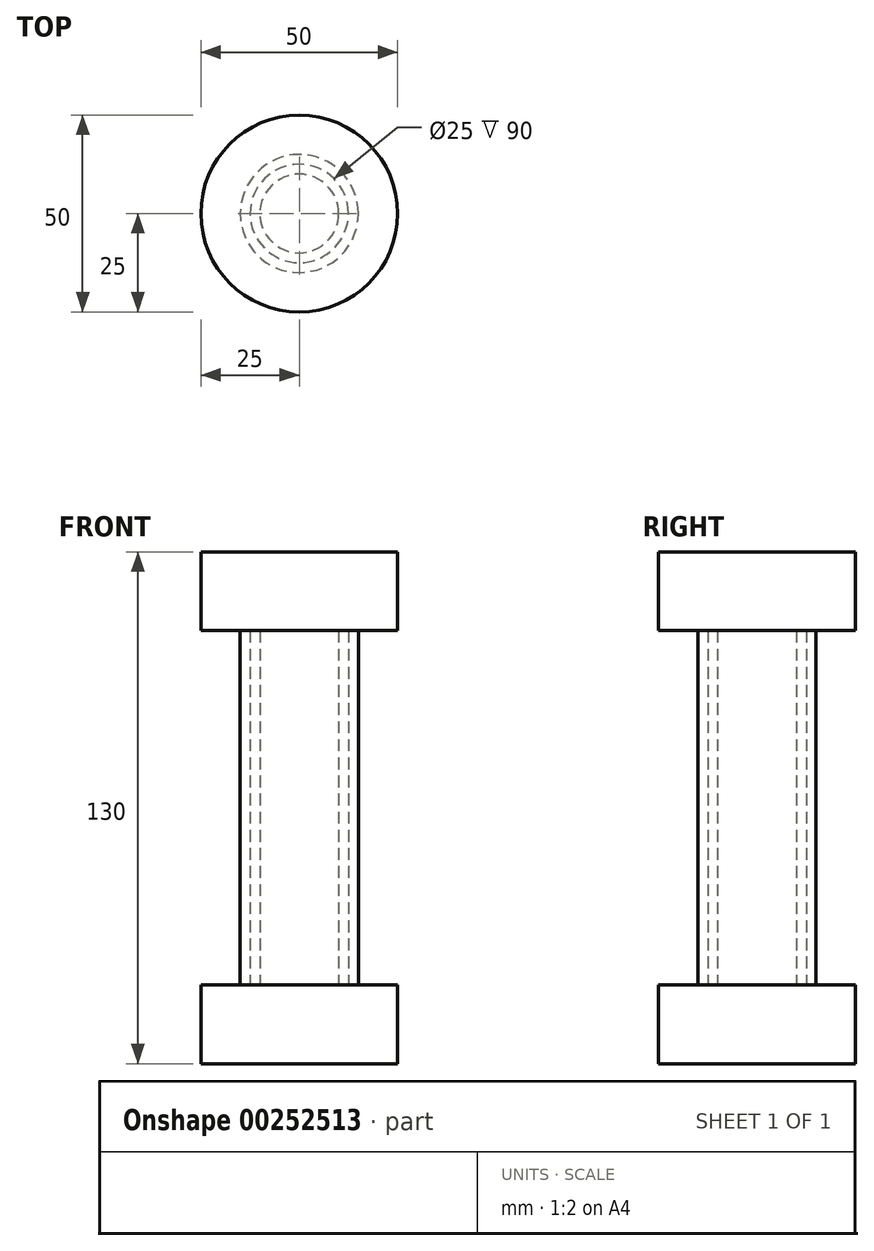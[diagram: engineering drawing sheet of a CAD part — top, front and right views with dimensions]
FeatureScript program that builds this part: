
annotation { "Feature Type Name" : "Feature", "Feature Type Description" : "" }
export const myFeature = defineFeature(function(context is Context, id is Id, definition is map)
    precondition{}
    {
        {
            var Q0;
            Q0=qCreatedBy(makeId("Top.planeOp"),FACE);
            var sketch = newSketch(context, id + "F0", { "sketchPlane" : qUnion([Q0])});
            skCircle(sketch, "E0", {"center": v(0, 0) * mm, "radius": 25 * mm});
            skSolve(sketch);
        }
        {
            var Q0;
            Q0 = qSketchRegion(id + "F0", true);
            extrude(context, id + "F1", {"entities" : qUnion([Q0]), "depth" : 20 * mm});
        }
        {
            var Q0;
            Q0=makeQuery(id+"F1.opExtrude","CAP_FACE",FACE,{"disambiguationData":[OSD([sQuery(id+"F0.wireOp",EDGE,"E0")])],"isStart":false});
            var sketch = newSketch(context, id + "F2", { "sketchPlane" : qUnion([Q0])});
            skCircle(sketch, "E1", {"center": v(0, 0) * mm, "radius": 15 * mm});
            skSolve(sketch);
        }
        {
            var Q0;
            Q0 = qSketchRegion(id + "F2", true);
            extrude(context, id + "F3", {"entities" : qUnion([Q0]), "operationType" : NewBodyOperationType.ADD, "depth" : 90 * mm});
        }
        {
            var Q0;
            Q0=makeQuery(id+"F3.opExtrude","CAP_FACE",FACE,{"disambiguationData":[OSD([sQuery(id+"F2.wireOp",EDGE,"E1")])],"isStart":false});
            var sketch = newSketch(context, id + "F4", { "sketchPlane" : qUnion([Q0])});
            skCircle(sketch, "E2", {"center": v(0, 0) * mm, "radius": 25 * mm});
            skSolve(sketch);
        }
        {
            var Q0;
            Q0 = qSketchRegion(id + "F4", true);
            extrude(context, id + "F5", {"entities" : qUnion([Q0]), "operationType" : NewBodyOperationType.ADD, "depth" : 20 * mm});
        }
        {
            var Q0;
            Q0=makeQuery(id+"F1.opExtrude","CAP_FACE",FACE,{"disambiguationData":[OSD([sQuery(id+"F0.wireOp",EDGE,"E0")])],"isStart":false});
            var sketch = newSketch(context, id + "F6", { "sketchPlane" : qUnion([Q0])});
            skCircle(sketch, "E3", {"center": v(0, 0) * mm, "radius": 12.5 * mm});
            skSolve(sketch);
        }
        {
            var Q0;
            Q0 = qSketchRegion(id + "F6", true);
            extrude(context, id + "F7", {"entities" : qUnion([Q0]), "operationType" : NewBodyOperationType.REMOVE, "depth" : 90 * mm});
        }
        {
            var Q0;
            Q0=makeQuery(id+"F1.opExtrude","CAP_FACE",FACE,{"disambiguationData":[OSD([sQuery(id+"F0.wireOp",EDGE,"E0")])],"isStart":false});
            var sketch = newSketch(context, id + "F8", { "sketchPlane" : qUnion([Q0])});
            skCircle(sketch, "E4", {"center": v(0, 0) * mm, "radius": 10 * mm});
            skSolve(sketch);
        }
        {
            var Q0;
            Q0 = qSketchRegion(id + "F8", true);
            extrude(context, id + "F9", {"entities" : qUnion([Q0]), "depth" : 90 * mm});
        }
        {
            var Q0;
            Q0=makeQuery(id+"F1.opExtrude","CAP_FACE",FACE,{"disambiguationData":[OSD([sQuery(id+"F0.wireOp",EDGE,"E0")])],"isStart":false});
            var sketch = newSketch(context, id + "F10", { "sketchPlane" : qUnion([Q0])});
            skCircle(sketch, "E5", {"center": v(0, 0) * mm, "radius": 9 * mm});
            skSolve(sketch);
        }
        {
            var Q0;
            Q0 = qSketchRegion(id + "F10", true);
            extrude(context, id + "F11", {"entities" : qUnion([Q0]), "operationType" : NewBodyOperationType.REMOVE, "depth" : 90 * mm});
        }
        {
            var Q0;
            Q0=makeQuery(id+"F9.opExtrude","CAP_FACE",FACE,{"disambiguationData":[OSD([sQuery(id+"F8.wireOp",EDGE,"E4")])],"isStart":true});
            var sketch = newSketch(context, id + "F12", { "sketchPlane" : qUnion([Q0])});
            skCircle(sketch, "E6", {"center": v(0, 0) * mm, "radius": 9 * mm});
            skSolve(sketch);
        }
        {
            var Q0;
            Q0 = qSketchRegion(id + "F12", true);
            extrude(context, id + "F13", {"entities" : qUnion([Q0]), "operationType" : NewBodyOperationType.ADD, "oppositeDirection" : true, "depth" : 90 * mm});
        }
    });
